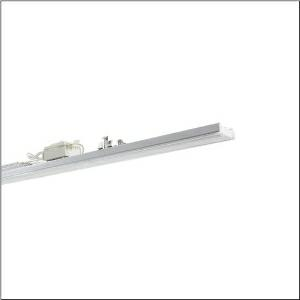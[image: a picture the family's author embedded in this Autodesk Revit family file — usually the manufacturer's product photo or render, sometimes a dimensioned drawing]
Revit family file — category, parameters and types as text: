
# Revit family: licross_11_recessed_ho_51tl12dn1d5m
name_source: partatom
category: Lighting Fixtures
units: mm (PartAtom-declared; Revit-internal decimal feet)

## family parameters
Cut with Voids When Loaded = No
Host = Face
Light Source = No
Part Type = Normal
Room Calculation Point = No
Round Connector Dimension = Use Diameter
Shared = No

## types (1)
- --- (1 x LED, 13580 lm, 76.8 W, 3500K)
    Apparent Load = 77 VA
    CIE Flux Codes = 66 91 98 100 100
    Color Rendering = 80
    Color Temperature = 3500K
    Default Elevation = 1800 mm
    Description = Licross 11 Recessed HO, luminaire insert, of sheet steel, coil coated, white, length: 1.500mm, width: 66mm, height: 67mm, LED rated luminous flux: 13.580lm, light colour: 835, SDCM (Standard Deviation of Colour Matching)MacAdam ≤ 2 SDCM (initial), control gear: DALI 2, with plug, 5-pole, with phase selection, mains connection: 220..240V, AC, 50/60Hz, rated input power: 77W, internal wiring halogen-free, primary optical cover: cover, of PMMA, light emission: direct distribution, primary light characteristic: symmetric, protection rating (complete): IP40, insulation class (complete): insulation class I (protective earthing), certification: CE, ENEC, VDE, UKCA, protection symbol: D if used in an environment without relevant dust loads with corresponding accessories, impact resistance: IK06, permissible ambient temperature for indoor applications: -25..+30°C, corresponds to IFS (International Featured Standards) requirements for safety and quality in the food industry, reducing of maximum allowable ambient temperature of 5°C with ceiling mounting, LABS conformity tested according to VDMA 24364:2018-05, The light source and the operating device comply with the requirements of the Ecodesign Regulation (EU) 2019/2020 and are replaceable in accordance with this regulation, packaging unit: 1 piece
    Height = 58 mm
    Lamp = 1 x LED
    Lamp Light Flux = 13580 lm
    Lamp Power = 76.8 W
    Lamp count = 1
    Length = 1500 mm
    Luminous efficacy = 177 lm/W
    Manufacturer = Siteco
    ModVariant = No
    Model = 51TL12DN1D5M
    Mounting Place = Ceiling
    Mounting Type = Pendant
    Number of Poles = 1
    OnlyDefault = Yes
    Power Factor = 1
    Product Name = Licross 11 Recessed HO
    Product group = luminaire insert | ceiling pendant
    ProductGroupID = 901
    Protection Class = Protection class I
    Protection Degree = IP 40
    RLX_Detail_Level = 1
    RLX_Emergency_Light_Flux = 0 lm
    RLX_Emergency_Type = 0
    RLX_Emergency_Type_DB = No
    RlxData = <blob elided: 24853 chars, md5=6d3a74ac>
    Socket = socket
    Standby Power = 0 W
    System Light Flux = 13580 lm
    System Power = 77 W
    Type Comments = factory setting: luminous flux: 100 % | dim-lin: 254 | 522 mA
    Type Image = l_1296930.jpg
    URL = http://relux.com
    VarID = @adj_075425
    Voltage = 0 V
    Weight = 0.00 kg
    Width = 66 mm

## geometry (parser evidence)
native form markers: Blend x4, Sweep x10
no freeform markers — native parametric forms only
